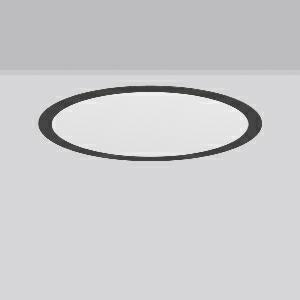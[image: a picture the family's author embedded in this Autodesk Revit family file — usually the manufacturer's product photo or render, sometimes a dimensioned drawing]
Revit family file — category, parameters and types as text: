
# Revit family: toledo_flat__round_e_901812_0031_2_76_f282
name_source: partatom
category: Lighting Fixtures
units: mm (PartAtom-declared; Revit-internal decimal feet)

## family parameters
Cut with Voids When Loaded = No
Host = Face
Light Source = No
Part Type = Normal
Room Calculation Point = No
Round Connector Dimension = Use Diameter
Shared = No

## types (1)
- TuneableWhite 827 (1 x LED Modul 827, 3150 lm, 2700)
    Apparent Load = 26 VA
    CIE Flux Codes = 47 79 96 100 100
    Color Rendering = 80
    Color Temperature = 2700
    Default Elevation = 1800 mm
    Description = Series: TOLEDO FLAT+ round
Flexible round recessed multifunction downlight. Housing: sheet steel, powder-coated. Luminaire frame: aluminium, powder-coated. Light guide and diffuser made of non-yellowing PMMA, opal matt. LED backlight technology for homogeneous illumination of the entire light-emitting surface. Tunable white dynamically adjustable from 2700 K to 6500 K. Suitable for Recessed ceiling mounting. Ceiling installation with spring system. Can be directly covered with thermal insulation material (applies only to the lower lumen levels). Including separate LED converter with connecting cable 250 mm. Surface mounted housing as accessory for all sizes. 
Colour: anthracite metallic (DB703)
Diameter: 470 mm
Height: 2 mm
Cut-out diameter: 457 mm
Recess height: 70 mm
Luminaire: recess height: 41 mm
Lamp: LED
Socket: without socket
Colour temperature: 2700K - 6500K
Colour rendering index (CRI): 80
System power: 26 W
Rated luminous flux: 3150 lm
Luminous efficiency: 121 lm/W
System power 2: 26 W
Rated luminous flux 2: 3300 lm
Luminous efficiency 2: 127 lm/W
System power 3: 26 W
Rated luminous flux 3: 3300 lm
Luminous efficiency 3: 127 lm/W
Control gear: Converter, dimmable, DALI
Protection class: II
Type of protection: IP 54
    Height = 0 mm  [stored 0 ft]
    Lamp = 1 x LED Modul 827
    Lamp Light Flux = 3150 lm
    Lamp count = 1
    Length = 470 mm
    Lifetime = 50000 h
    Luminous efficacy = 121 lm/W
    Manufacturer = RZB
    ModVariant = No
    Model = 901812.0031.2.76
    Mounting Place = Ceiling
    Mounting Type = Recessed
    Number of Poles = 1
    OnlyDefault = Yes
    Power Factor = 1
    Product Name = TOLEDO FLAT+ round E
    Product group = Recessed downlights
    ProductGroupID = 402
    Protection Class = Protection class II
    Protection Degree = Degree of protection
    RLX_Detail_Level = 1
    RLX_Emergency_Light_Flux = 0 lm
    RLX_Emergency_Type = 0
    RLX_Emergency_Type_DB = No
    RlxData = <blob elided: 40097 chars, md5=74553364>
    Socket = socket
    Standby Power = 0 W
    System Light Flux = 3150 lm
    System Power = 26 W
    Type Comments = TuneableWhite 827
    Type Image = 901812.0031.jpg
    URL = http://relux.com
    VarID = tuneablewhite_827
    Voltage = 0 V
    Weight = 0.00 kg
    Width = 0 mm  [stored 0 ft]

note: [stored X ft] marks values corroborated as IEEE doubles in the binary element streams (Revit-internal decimal feet)

## geometry (parser evidence)
native form markers: Blend x4, Sweep x9
no freeform markers — native parametric forms only
